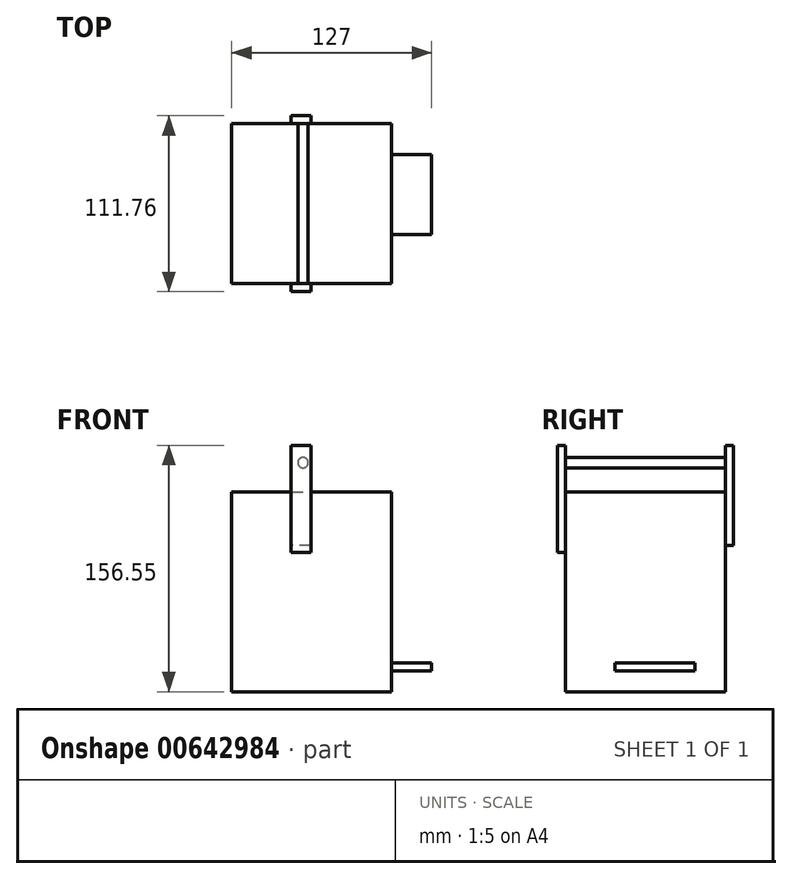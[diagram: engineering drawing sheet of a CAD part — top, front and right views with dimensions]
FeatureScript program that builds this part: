
annotation { "Feature Type Name" : "Feature", "Feature Type Description" : "" }
export const myFeature = defineFeature(function(context is Context, id is Id, definition is map)
    precondition{}
    {
        {
            var Q0;
            Q0=qCreatedBy(makeId("Front.planeOp"),FACE);
            var sketch = newSketch(context, id + "F0", { "sketchPlane" : qUnion([Q0])});
            skLineSegment(sketch, "E0", {"start": v(0, 0) * mm, "end": v(-101.6, 0) * mm});
            skLineSegment(sketch, "E1", {"start": v(-101.6, 0) * mm, "end": v(-101.6, 127) * mm});
            skLineSegment(sketch, "E2", {"start": v(-101.6, 127) * mm, "end": v(0, 127) * mm});
            skLineSegment(sketch, "E3", {"start": v(0, 127) * mm, "end": v(0, 0) * mm});
            skSolve(sketch);
        }
        {
            var Q0;
            Q0 = qSketchRegion(id + "F0", true);
            extrude(context, id + "F1", {"entities" : qUnion([Q0]), "depth" : 101.6 * mm, "offsetDistance" : 25.4 * mm});
        }
        {
            var Q0;
            Q0=makeQuery(id+"F1.opExtrude","SWEPT_FACE",FACE,{"disambiguationData":[OSD([sQuery(id+"F0.wireOp",EDGE,"E3")])]});
            var sketch = newSketch(context, id + "F2", { "sketchPlane" : qUnion([Q0])});
            skLineSegment(sketch, "E4", {"start": v(-70.2, 18.37) * mm, "end": v(-19.4, 18.37) * mm});
            skLineSegment(sketch, "E5", {"start": v(-19.4, 18.37) * mm, "end": v(-19.4, 13.3) * mm});
            skLineSegment(sketch, "E6", {"start": v(-19.4, 13.3) * mm, "end": v(-70.2, 13.3) * mm});
            skLineSegment(sketch, "E7", {"start": v(-70.2, 18.37) * mm, "end": v(-70.2, 13.3) * mm});
            skSolve(sketch);
        }
        {
            var Q0;
            Q0=makeQuery(id+"F2.imprint","IMPRINT",FACE,{"disambiguationData":[TD([[makeQuery(id+"F2.imprint","IMPRINT",EDGE,{"derivedFrom":sQuery(id+"F2.wireOp",EDGE,"E4")}),-1.0]])]});
            extrude(context, id + "F3", {"entities" : qUnion([Q0]), "operationType" : NewBodyOperationType.ADD, "depth" : 25.4 * mm, "offsetDistance" : 25.4 * mm});
        }
        {
            var Q0;
            Q0=makeQuery(id+"F1.opExtrude","CAP_FACE",FACE,{"disambiguationData":[OSD([sQuery(id+"F0.wireOp",EDGE,"E0"),sQuery(id+"F0.wireOp",EDGE,"E1"),sQuery(id+"F0.wireOp",EDGE,"E2"),sQuery(id+"F0.wireOp",EDGE,"E3")])],"isStart":false});
            var sketch = newSketch(context, id + "F4", { "sketchPlane" : qUnion([Q0])});
            skLineSegment(sketch, "E8", {"start": v(-63.83, 156.55) * mm, "end": v(-51.13, 156.55) * mm});
            skLineSegment(sketch, "E9", {"start": v(-51.13, 156.55) * mm, "end": v(-51.13, 88.47) * mm});
            skLineSegment(sketch, "E10", {"start": v(-51.13, 88.47) * mm, "end": v(-63.83, 88.47) * mm});
            skLineSegment(sketch, "E11", {"start": v(-63.83, 156.55) * mm, "end": v(-63.83, 88.47) * mm});
            skSolve(sketch);
        }
        {
            var Q0;
            {var subQ0=sQuery(id+"F4.wireOp",EDGE,"E8");Q0=makeQuery(id+"F4.imprint","IMPRINT",FACE,{"disambiguationData":[TD([[makeQuery(id+"F4.imprint","IMPRINT",EDGE,{"derivedFrom":subQ0}),-1.0]])]});}
            var Q1;
            {var subQ0=sQuery(id+"F4.wireOp",EDGE,"E10");Q1=makeQuery(id+"F4.imprint","IMPRINT",FACE,{"disambiguationData":[TD([[makeQuery(id+"F4.imprint","IMPRINT",EDGE,{"derivedFrom":subQ0}),-1.0]])]});}
            extrude(context, id + "F5", {"entities" : qUnion([Q0, Q1]), "operationType" : NewBodyOperationType.ADD, "depth" : 5.08 * mm, "offsetDistance" : 25.4 * mm});
        }
        {
            var Q0;
            Q0=makeQuery(id+"F1.opExtrude","CAP_FACE",FACE,{"disambiguationData":[OSD([sQuery(id+"F0.wireOp",EDGE,"E0"),sQuery(id+"F0.wireOp",EDGE,"E1"),sQuery(id+"F0.wireOp",EDGE,"E2"),sQuery(id+"F0.wireOp",EDGE,"E3")])],"isStart":true});
            var sketch = newSketch(context, id + "F6", { "sketchPlane" : qUnion([Q0])});
            skPoint(sketch, "E12.0", {"position": v(51.13, 156.55) * mm});
            skPoint(sketch, "E13.0", {"position": v(63.83, 156.55) * mm});
            skLineSegment(sketch, "E14", {"start": v(51.13, 156.55) * mm, "end": v(51.13, 93.05) * mm});
            skLineSegment(sketch, "E15", {"start": v(51.13, 93.05) * mm, "end": v(63.83, 93.05) * mm});
            skLineSegment(sketch, "E16", {"start": v(63.83, 93.05) * mm, "end": v(63.83, 156.55) * mm});
            skLineSegment(sketch, "E17", {"start": v(51.13, 156.55) * mm, "end": v(63.83, 156.55) * mm});
            skLineSegment(sketch, "E18", {"start": v(63.83, 93.05) * mm, "end": v(51.13, 93.05) * mm});
            skSolve(sketch);
        }
        {
            var Q0;
            Q0 = qSketchRegion(id + "F6", true);
            extrude(context, id + "F7", {"entities" : qUnion([Q0]), "operationType" : NewBodyOperationType.ADD, "depth" : 5.08 * mm, "offsetDistance" : 25.4 * mm});
        }
        {
            var Q0;
            Q0=makeQuery(id+"F7.opExtrude","CAP_FACE",FACE,{"disambiguationData":[OSD([sQuery(id+"F6.wireOp",EDGE,"E16"),sQuery(id+"F6.wireOp",EDGE,"E17"),sQuery(id+"F6.wireOp",EDGE,"E18"),sQuery(id+"F6.wireOp",EDGE,"E14")])],"isStart":false});
            var sketch = newSketch(context, id + "F8", { "sketchPlane" : qUnion([Q0])});
            skCircle(sketch, "E19", {"center": v(56.34, 145.5) * mm, "radius": 3.31 * mm});
            skSolve(sketch);
        }
        {
            var Q0;
            Q0=makeQuery(id+"F8.imprint","IMPRINT",FACE,{"disambiguationData":[TD([[makeQuery(id+"F8.imprint","IMPRINT",EDGE,{"derivedFrom":sQuery(id+"F8.wireOp",EDGE,"E19")}),1.0]])]});
            extrude(context, id + "F9", {"entities" : qUnion([Q0]), "operationType" : NewBodyOperationType.ADD, "oppositeDirection" : true, "depth" : 109.22 * mm, "offsetDistance" : 25.4 * mm});
        }
    });
